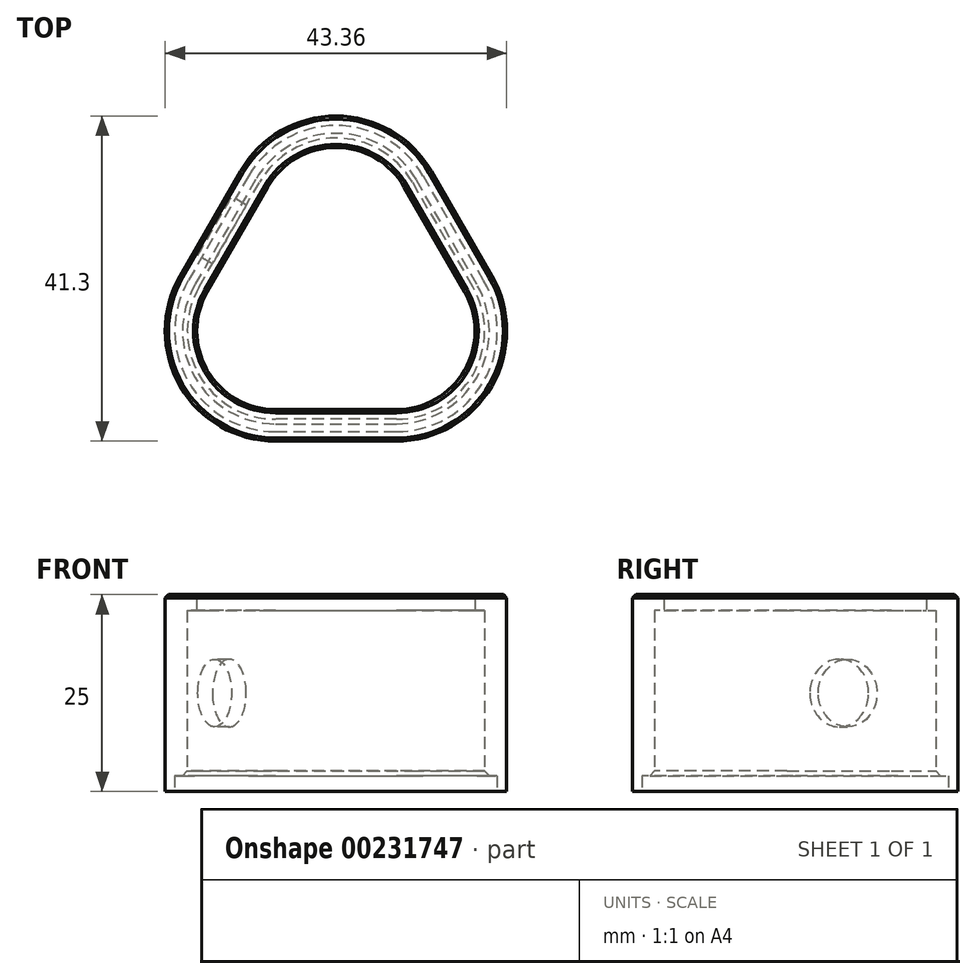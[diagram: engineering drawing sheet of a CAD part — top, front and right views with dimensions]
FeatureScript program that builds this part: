
annotation { "Feature Type Name" : "Feature", "Feature Type Description" : "" }
export const myFeature = defineFeature(function(context is Context, id is Id, definition is map)
    precondition{}
    {
        {
            var Q0;
            Q0=qCreatedBy(makeId("Top.planeOp"),FACE);
            var sketch = newSketch(context, id + "F0", { "sketchPlane" : qUnion([Q0])});
            skLineSegment(sketch, "E0", {"start": v(0, 0) * mm, "end": v(7.68, 0) * mm});
            skLineSegment(sketch, "E1", {"start": v(16.34, 15) * mm, "end": v(8.66, 28.3) * mm});
            skLineSegment(sketch, "E2", {"start": v(-8.66, 28.3) * mm, "end": v(-16.34, 15) * mm});
            skLineSegment(sketch, "E3", {"start": v(-7.68, 0) * mm, "end": v(0, 0) * mm});
            skLineSegment(sketch, "E4", {"start": v(0, 0) * mm, "end": v(0, 43.3) * mm, "construction": true});
            skLineSegment(sketch, "E5", {"start": v(-12.5, 21.65) * mm, "end": v(25, 0) * mm, "construction": true});
            skLineSegment(sketch, "E6", {"start": v(12.5, 21.65) * mm, "end": v(-25, 0) * mm, "construction": true});
            skCircle(sketch, "E7", {"center": v(0, 14.43) * mm, "radius": 12.5 * mm});
            skPoint(sketch, "E8.visualSharp", {"position": v(0, 43.3) * mm});
            skArc(sketch, "E8.filletArc", {"start": v(8.66, 28.3) * mm, "mid": v(0, 33.3) * mm, "end": v(-8.66, 28.3) * mm});
            skPoint(sketch, "E9.visualSharp", {"position": v(-25, 0) * mm});
            skArc(sketch, "E9.filletArc", {"start": v(-16.34, 15) * mm, "mid": v(-16.34, 5) * mm, "end": v(-7.68, 0) * mm});
            skPoint(sketch, "E10.visualSharp", {"position": v(25, 0) * mm});
            skArc(sketch, "E10.filletArc", {"start": v(7.68, 0) * mm, "mid": v(16.34, 5) * mm, "end": v(16.34, 15) * mm});
            skLineSegment(sketch, "E11.0", {"start": v(19.8, 17) * mm, "end": v(12.12, 30.3) * mm});
            skArc(sketch, "E11.1", {"start": v(7.68, -4) * mm, "mid": v(19.8, 3) * mm, "end": v(19.8, 17) * mm});
            skLineSegment(sketch, "E11.2", {"start": v(-12.12, 30.3) * mm, "end": v(-19.8, 17) * mm});
            skArc(sketch, "E11.3", {"start": v(-19.8, 17) * mm, "mid": v(-19.8, 3) * mm, "end": v(-7.68, -4) * mm});
            skLineSegment(sketch, "E11.4", {"start": v(-7.68, -4) * mm, "end": v(0, -4) * mm});
            skArc(sketch, "E11.5", {"start": v(12.12, 30.3) * mm, "mid": v(0, 37.3) * mm, "end": v(-12.12, 30.3) * mm});
            skLineSegment(sketch, "E11.6", {"start": v(0, -4) * mm, "end": v(7.68, -4) * mm});
            skSolve(sketch);
        }
        {
            var Q0;
            Q0=makeQuery(id+"F0.imprint","IMPRINT",FACE,{"disambiguationData":[TD([[makeQuery(id+"F0.imprint","IMPRINT",EDGE,{"derivedFrom":sQuery(id+"F0.wireOp",EDGE,"E0")}),-1.0]])]});
            extrude(context, id + "F1", {"entities" : qUnion([Q0]), "depth" : 25 * mm});
        }
        {
            var Q0;
            Q0=makeQuery(id+"F1.opExtrude","SWEPT_FACE",FACE,{"disambiguationData":[OSD([sQuery(id+"F0.wireOp",EDGE,"E11.2")])]});
            var sketch = newSketch(context, id + "F2", { "sketchPlane" : qUnion([Q0])});
            skCircle(sketch, "E12", {"center": v(-12.5, 12.5) * mm, "radius": 4.3 * mm});
            skPoint(sketch, "E12.centerSnap0", {"position": v(-12.5, 25) * mm});
            skPoint(sketch, "E12.centerSnap1", {"position": v(-20.18, 12.5) * mm});
            skSolve(sketch);
        }
        {
            var Q0;
            Q0 = qSketchRegion(id + "F2", true);
            extrude(context, id + "F3", {"entities" : qUnion([Q0]), "operationType" : NewBodyOperationType.REMOVE, "oppositeDirection" : true, "depth" : 2.8 * mm, "hasSecondDirection" : true, "secondDirectionOppositeDirection" : true, "secondDirectionDepth" : 0.65 * mm});
        }
        {
            var Q0;
            Q0=makeQuery(id+"F1.opExtrude","CAP_FACE",FACE,{"disambiguationData":[OSD([sQuery(id+"F0.wireOp",EDGE,"E0"),sQuery(id+"F0.wireOp",EDGE,"E1"),sQuery(id+"F0.wireOp",EDGE,"E2"),sQuery(id+"F0.wireOp",EDGE,"E3"),sQuery(id+"F0.wireOp",EDGE,"E8.filletArc"),sQuery(id+"F0.wireOp",EDGE,"E9.filletArc"),sQuery(id+"F0.wireOp",EDGE,"E10.filletArc"),sQuery(id+"F0.wireOp",EDGE,"E11.0"),sQuery(id+"F0.wireOp",EDGE,"E11.1"),sQuery(id+"F0.wireOp",EDGE,"E11.2"),sQuery(id+"F0.wireOp",EDGE,"E11.3"),sQuery(id+"F0.wireOp",EDGE,"E11.4"),sQuery(id+"F0.wireOp",EDGE,"E11.5"),sQuery(id+"F0.wireOp",EDGE,"E11.6")])],"isStart":false});
            var sketch = newSketch(context, id + "F4", { "sketchPlane" : qUnion([Q0])});
            skLineSegment(sketch, "E13", {"start": v(-12.5, 21.65) * mm, "end": v(16.34, 5) * mm});
            skLineSegment(sketch, "E14", {"start": v(16.34, 5) * mm, "end": v(0, 0) * mm});
            skLineSegment(sketch, "E15", {"start": v(0, 0) * mm, "end": v(0, 33.3) * mm});
            skCircle(sketch, "E16", {"center": v(0, 14.43) * mm, "radius": 3.2 * mm});
            skSolve(sketch);
        }
        {
            var Q0;
            Q0=makeQuery(id+"F1.opExtrude","CAP_FACE",FACE,{"disambiguationData":[OSD([sQuery(id+"F0.wireOp",EDGE,"E0"),sQuery(id+"F0.wireOp",EDGE,"E1"),sQuery(id+"F0.wireOp",EDGE,"E2"),sQuery(id+"F0.wireOp",EDGE,"E3"),sQuery(id+"F0.wireOp",EDGE,"E8.filletArc"),sQuery(id+"F0.wireOp",EDGE,"E9.filletArc"),sQuery(id+"F0.wireOp",EDGE,"E10.filletArc"),sQuery(id+"F0.wireOp",EDGE,"E11.0"),sQuery(id+"F0.wireOp",EDGE,"E11.1"),sQuery(id+"F0.wireOp",EDGE,"E11.2"),sQuery(id+"F0.wireOp",EDGE,"E11.3"),sQuery(id+"F0.wireOp",EDGE,"E11.4"),sQuery(id+"F0.wireOp",EDGE,"E11.5"),sQuery(id+"F0.wireOp",EDGE,"E11.6")])],"isStart":true});
            var sketch = newSketch(context, id + "F5", { "sketchPlane" : qUnion([Q0])});
            skLineSegment(sketch, "E17.0", {"start": v(17.38, -15.6) * mm, "end": v(9.7, -28.9) * mm});
            skLineSegment(sketch, "E17.1", {"start": v(-9.7, -28.9) * mm, "end": v(-17.38, -15.6) * mm});
            skArc(sketch, "E17.2", {"start": v(-17.38, -15.6) * mm, "mid": v(-17.38, -4.4) * mm, "end": v(-7.68, 1.2) * mm});
            skArc(sketch, "E17.3", {"start": v(9.7, -28.9) * mm, "mid": v(0, -34.5) * mm, "end": v(-9.7, -28.9) * mm});
            skLineSegment(sketch, "E17.4", {"start": v(-7.68, 1.2) * mm, "end": v(7.68, 1.2) * mm});
            skArc(sketch, "E17.5", {"start": v(7.68, 1.2) * mm, "mid": v(17.38, -4.4) * mm, "end": v(17.38, -15.6) * mm});
            skSolve(sketch);
        }
        {
            var Q0;
            Q0 = qSketchRegion(id + "F5", true);
            extrude(context, id + "F6", {"entities" : qUnion([Q0]), "operationType" : NewBodyOperationType.REMOVE, "oppositeDirection" : true, "depth" : 23 * mm});
        }
        {
            var Q0;
            Q0=makeQuery(id+"F1.opExtrude","CAP_FACE",FACE,{"disambiguationData":[OSD([sQuery(id+"F0.wireOp",EDGE,"E0"),sQuery(id+"F0.wireOp",EDGE,"E1"),sQuery(id+"F0.wireOp",EDGE,"E2"),sQuery(id+"F0.wireOp",EDGE,"E3"),sQuery(id+"F0.wireOp",EDGE,"E8.filletArc"),sQuery(id+"F0.wireOp",EDGE,"E9.filletArc"),sQuery(id+"F0.wireOp",EDGE,"E10.filletArc"),sQuery(id+"F0.wireOp",EDGE,"E11.0"),sQuery(id+"F0.wireOp",EDGE,"E11.1"),sQuery(id+"F0.wireOp",EDGE,"E11.2"),sQuery(id+"F0.wireOp",EDGE,"E11.3"),sQuery(id+"F0.wireOp",EDGE,"E11.4"),sQuery(id+"F0.wireOp",EDGE,"E11.5"),sQuery(id+"F0.wireOp",EDGE,"E11.6")])],"isStart":true});
            var sketch = newSketch(context, id + "F7", { "sketchPlane" : qUnion([Q0])});
            skLineSegment(sketch, "E18.0", {"start": v(18.76, -16.4) * mm, "end": v(11.09, -29.7) * mm});
            skLineSegment(sketch, "E18.1", {"start": v(-11.09, -29.7) * mm, "end": v(-18.76, -16.4) * mm});
            skArc(sketch, "E18.2", {"start": v(-18.76, -16.4) * mm, "mid": v(-18.76, -3.6) * mm, "end": v(-7.68, 2.8) * mm});
            skArc(sketch, "E18.3", {"start": v(11.09, -29.7) * mm, "mid": v(0, -36.1) * mm, "end": v(-11.09, -29.7) * mm});
            skLineSegment(sketch, "E18.4", {"start": v(-7.68, 2.8) * mm, "end": v(7.68, 2.8) * mm});
            skArc(sketch, "E18.5", {"start": v(7.68, 2.8) * mm, "mid": v(18.76, -3.6) * mm, "end": v(18.76, -16.4) * mm});
            skSolve(sketch);
        }
        {
            var Q0;
            Q0 = qSketchRegion(id + "F7", true);
            extrude(context, id + "F8", {"entities" : qUnion([Q0]), "operationType" : NewBodyOperationType.REMOVE, "oppositeDirection" : true, "depth" : 2 * mm});
        }
        {
            var Q0;
            Q0=makeQuery(id+"F8.boolean.opBoolean","INTERSECT",EDGE,{"derivedFrom":[makeQuery(id+"F6.boolean.opBoolean","COPY",FACE,{"derivedFrom":makeQuery(id+"F6.opExtrude","SWEPT_FACE",FACE,{"disambiguationData":[OSD([sQuery(id+"F5.wireOp",EDGE,"E17.3")])]})}),makeQuery(id+"F8.opExtrude","CAP_FACE",FACE,{"disambiguationData":[OSD([sQuery(id+"F7.wireOp",EDGE,"E18.0"),sQuery(id+"F7.wireOp",EDGE,"E18.1"),sQuery(id+"F7.wireOp",EDGE,"E18.2"),sQuery(id+"F7.wireOp",EDGE,"E18.3"),sQuery(id+"F7.wireOp",EDGE,"E18.4"),sQuery(id+"F7.wireOp",EDGE,"E18.5")])],"isStart":false})]});
            chamfer(context, id + "F9", {"entities" : qUnion([Q0]), "width" : 0.6 * mm, "tangentPropagation" : true});
        }
        {
            var Q0;
            Q0=makeQuery(id+"F1.opExtrude","CAP_EDGE",EDGE,{"disambiguationData":[OSD([sQuery(id+"F0.wireOp",EDGE,"E11.1")])],"isStart":false});
            var Q1;
            Q1=makeQuery(id+"F1.opExtrude","CAP_EDGE",EDGE,{"disambiguationData":[OSD([sQuery(id+"F0.wireOp",EDGE,"E1")])],"isStart":false});
            chamfer(context, id + "F10", {"entities" : qUnion([Q0, Q1]), "width" : 0.4 * mm, "tangentPropagation" : true});
        }
    });
